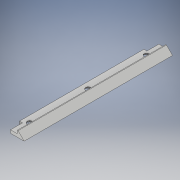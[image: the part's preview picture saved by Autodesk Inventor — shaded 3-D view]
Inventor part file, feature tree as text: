
AUTODESK INVENTOR PART (.ipt)
format: ipt  version: 2019 (Build 230136000, 136)  size: 142,336 bytes
history: native  units: mm
features: sketch x3, extrude x2, other x1, hole x1
ambient origin geometry x8: Origin, YZ Plane, XZ Plane, XY Plane, X Axis, Y Axis, Z Axis, Center Point
bodies: Body1 (feature_tree)
feature tree (7):
  other  "Bryła1"
  extrude  "Wyciągnięcie proste1"  TaperAngle=45.0deg  [1 undecoded]
  hole  "Otwór1"  [1 undecoded]
  extrude  "Wyciągnięcie proste2"  Depth=2.0mm
  sketch  "Szkic1"
  sketch  "Szkic4"
  sketch  "Szkic5"
note: 2 required parameter values undecoded (feature->parameter linkage not recoverable at this tier; creation-order binding heuristic only, values carry confidence <= 0.55)
